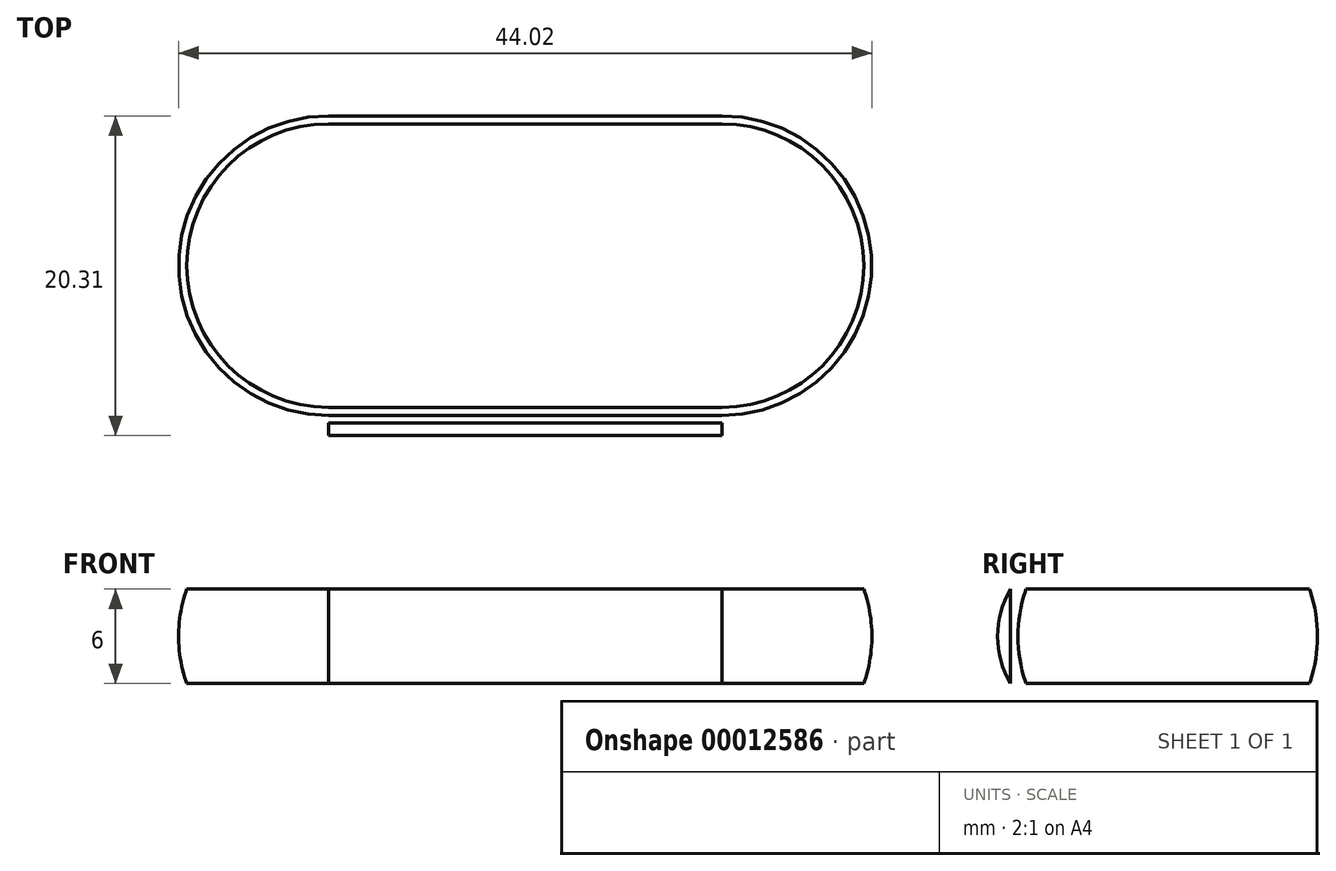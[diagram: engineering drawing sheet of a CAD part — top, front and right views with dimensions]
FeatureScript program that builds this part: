
annotation { "Feature Type Name" : "Feature", "Feature Type Description" : "" }
export const myFeature = defineFeature(function(context is Context, id is Id, definition is map)
    precondition{}
    {
        {
            var Q0;
            Q0=qCreatedBy(makeId("Top.planeOp"),FACE);
            var sketch = newSketch(context, id + "F0", { "sketchPlane" : qUnion([Q0])});
            skLineSegment(sketch, "E0.rect.bottom", {"start": v(12.5, 10) * mm, "end": v(-12.5, 10) * mm});
            skLineSegment(sketch, "E0.rect.top", {"start": v(12.5, -10) * mm, "end": v(-12.5, -10) * mm});
            skLineSegment(sketch, "E0.rect.left", {"start": v(22.5, 0) * mm, "end": v(22.5, 0) * mm});
            skLineSegment(sketch, "E0.rect.right", {"start": v(-22.5, 0) * mm, "end": v(-22.5, 0) * mm});
            skPoint(sketch, "E0.rect.middle", {"position": v(0, 0) * mm});
            skPoint(sketch, "E1.visualSharp", {"position": v(-22.5, 10) * mm});
            skArc(sketch, "E1.filletArc", {"start": v(-12.5, 10) * mm, "mid": v(-19.57, 7.07) * mm, "end": v(-22.5, 0) * mm});
            skPoint(sketch, "E2.visualSharp", {"position": v(-22.5, -10) * mm});
            skArc(sketch, "E2.filletArc", {"start": v(-22.5, 0) * mm, "mid": v(-19.57, -7.07) * mm, "end": v(-12.5, -10) * mm});
            skPoint(sketch, "E3.visualSharp", {"position": v(22.5, -10) * mm});
            skArc(sketch, "E3.filletArc", {"start": v(12.5, -10) * mm, "mid": v(19.57, -7.07) * mm, "end": v(22.5, 0) * mm});
            skPoint(sketch, "E4.visualSharp", {"position": v(22.5, 10) * mm});
            skArc(sketch, "E4.filletArc", {"start": v(22.5, 0) * mm, "mid": v(19.57, 7.07) * mm, "end": v(12.5, 10) * mm});
            skSolve(sketch);
        }
        {
            var Q0;
            Q0 = qSketchRegion(id + "F0", true);
            extrude(context, id + "F1", {"entities" : qUnion([Q0]), "depth" : 6 * mm});
        }
        {
            var Q0;
            Q0=makeQuery(id+"F1.opExtrude","CAP_FACE",FACE,{"disambiguationData":[OSD([sQuery(id+"F0.wireOp",EDGE,"E0.rect.bottom"),sQuery(id+"F0.wireOp",EDGE,"E0.rect.top"),sQuery(id+"F0.wireOp",EDGE,"E1.filletArc"),sQuery(id+"F0.wireOp",EDGE,"E2.filletArc"),sQuery(id+"F0.wireOp",EDGE,"E3.filletArc"),sQuery(id+"F0.wireOp",EDGE,"E4.filletArc")])],"isStart":false});
            var sketch = newSketch(context, id + "F2", { "sketchPlane" : qUnion([Q0])});
            skArc(sketch, "E5.0", {"start": v(12.5, -8) * mm, "mid": v(20.5, 0) * mm, "end": v(12.5, 8) * mm});
            skLineSegment(sketch, "E5.1", {"start": v(-12.5, -8) * mm, "end": v(12.5, -8) * mm});
            skArc(sketch, "E5.2", {"start": v(-12.5, 8) * mm, "mid": v(-20.5, 0) * mm, "end": v(-12.5, -8) * mm});
            skLineSegment(sketch, "E5.3", {"start": v(12.5, 8) * mm, "end": v(-12.5, 8) * mm});
            skSolve(sketch);
        }
        {
            var Q0;
            Q0=qCreatedBy(makeId("Right.planeOp"),FACE);
            var sketch = newSketch(context, id + "F3", { "sketchPlane" : qUnion([Q0])});
            skLineSegment(sketch, "E6.0", {"start": v(-10, 0) * mm, "end": v(10, 0) * mm, "construction": true});
            skLineSegment(sketch, "E7.0", {"start": v(-8, 6) * mm, "end": v(8, 6) * mm, "construction": true});
            skLineSegment(sketch, "E8", {"start": v(-8, 6) * mm, "end": v(-8, 0) * mm, "construction": true});
            skArc(sketch, "E9", {"start": v(-8, 6) * mm, "mid": v(-8.8, 3) * mm, "end": v(-8, 0) * mm});
            skLineSegment(sketch, "E10", {"start": v(-8, 6) * mm, "end": v(-8, 11.82) * mm});
            skLineSegment(sketch, "E11", {"start": v(-8, 11.82) * mm, "end": v(-15.06, 11.82) * mm});
            skLineSegment(sketch, "E12", {"start": v(-15.06, 11.82) * mm, "end": v(-15.06, -3.9) * mm});
            skLineSegment(sketch, "E13", {"start": v(-15.06, -3.9) * mm, "end": v(-7.87, -3.9) * mm});
            skLineSegment(sketch, "E14", {"start": v(-7.87, -3.9) * mm, "end": v(-8, 0) * mm});
            skSolve(sketch);
        }
        {
            var Q0;
            Q0=qCreatedBy(makeId("Right.planeOp"),FACE);
            var sketch = newSketch(context, id + "F4", { "sketchPlane" : qUnion([Q0])});
            skLineSegment(sketch, "E15.0", {"start": v(-10, 6) * mm, "end": v(10, 6) * mm, "construction": true});
            skLineSegment(sketch, "E16.0", {"start": v(-10, 0) * mm, "end": v(10, 0) * mm, "construction": true});
            skArc(sketch, "E17", {"start": v(-10, 6) * mm, "mid": v(-10.8, 3) * mm, "end": v(-10, 0) * mm});
            skLineSegment(sketch, "E18", {"start": v(-10, 6) * mm, "end": v(-10, 0) * mm});
            skSolve(sketch);
        }
        {
            var Q0;
            Q0=makeQuery(id+"F1.opExtrude","CAP_FACE",FACE,{"disambiguationData":[OSD([sQuery(id+"F0.wireOp",EDGE,"E0.rect.bottom"),sQuery(id+"F0.wireOp",EDGE,"E0.rect.top"),sQuery(id+"F0.wireOp",EDGE,"E1.filletArc"),sQuery(id+"F0.wireOp",EDGE,"E2.filletArc"),sQuery(id+"F0.wireOp",EDGE,"E3.filletArc"),sQuery(id+"F0.wireOp",EDGE,"E4.filletArc")])],"isStart":false});
            var sketch = newSketch(context, id + "F5", { "sketchPlane" : qUnion([Q0])});
            skArc(sketch, "E19.0.0", {"start": v(12.5, -10) * mm, "mid": v(22.5, 0) * mm, "end": v(12.5, 10) * mm});
            skLineSegment(sketch, "E19.0.1", {"start": v(12.5, 10) * mm, "end": v(-12.5, 10) * mm});
            skArc(sketch, "E19.0.2", {"start": v(-12.5, 10) * mm, "mid": v(-22.5, 0) * mm, "end": v(-12.5, -10) * mm});
            skLineSegment(sketch, "E19.0.3", {"start": v(-12.5, -10) * mm, "end": v(12.5, -10) * mm});
            skSolve(sketch);
        }
        {
            var Q0;
            Q0=makeQuery(id+"F4.imprint","IMPRINT",FACE,{"disambiguationData":[TD([[makeQuery(id+"F4.imprint","IMPRINT",EDGE,{"derivedFrom":sQuery(id+"F4.wireOp",EDGE,"E17")}),1.0]])]});
            var Q1;
            Q1=sQuery(id+"F5.wireOp",EDGE,"E19.0.3");
            sweep(context, id + "F6", {"profiles" : qUnion([Q0]), "path" : qUnion([Q1])});
        }
        {
            var Q0;
            Q0=makeQuery(id+"F1.opExtrude","CAP_EDGE",EDGE,{"disambiguationData":[OSD([sQuery(id+"F0.wireOp",EDGE,"E0.rect.top")])],"isStart":false});
            var Q1;
            Q1=makeQuery(id+"F1.opExtrude","CAP_EDGE",EDGE,{"disambiguationData":[OSD([sQuery(id+"F0.wireOp",EDGE,"E0.rect.top")])],"isStart":true});
            chamfer(context, id + "F7", {"entities" : qUnion([Q0, Q1]), "chamferType" : ChamferType.TWO_OFFSETS, "width1" : 3 * mm, "oppositeDirection" : false, "width2" : 1 * mm, "tangentPropagation" : true});
        }
        {
            var Q0;
            {var subQ0=sQuery(id+"F0.wireOp",EDGE,"E3.filletArc");var subQ1=sQuery(id+"F0.wireOp",EDGE,"E4.filletArc");Q0=makeQuery(id+"F7.opChamfer","BLEND_EDGE",EDGE,{"blendedFrom":[makeQuery(id+"F1.opExtrude","CAP_EDGE",EDGE,{"disambiguationData":[OSD([subQ0,subQ1])],"isStart":true}),makeQuery(id+"F1.opExtrude","CAP_EDGE",EDGE,{"disambiguationData":[OSD([subQ0,subQ1])],"isStart":false})],"blendedInto":[]});}
            fillet(context, id + "F8", {"entities" : qUnion([Q0]), "radius" : 9 * mm, "tangentPropagation" : true, "allowEdgeOverflow" : false});
        }
    });
